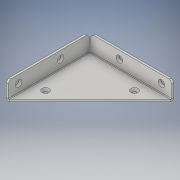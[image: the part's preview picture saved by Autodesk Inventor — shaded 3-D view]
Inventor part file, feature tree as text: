
AUTODESK INVENTOR PART (.ipt)
format: ipt  version: 2018 (Build 220112000, 112)  size: 165,888 bytes
history: native  units: in
note: dims shown in document units (in); Inventor stores cm internally (conversion verified against a paired STEP export)
features: chamfer x1
ambient origin geometry x8: Origin, YZ Plane, XZ Plane, XY Plane, X Axis, Y Axis, Z Axis, Center Point
bodies: Solid1 (feature_tree)
feature tree (1):
  chamfer  "Chamfer3"  [1 undecoded]
note: 1 required parameter value undecoded (feature->parameter linkage not recoverable at this tier; creation-order binding heuristic only, values carry confidence <= 0.55)
